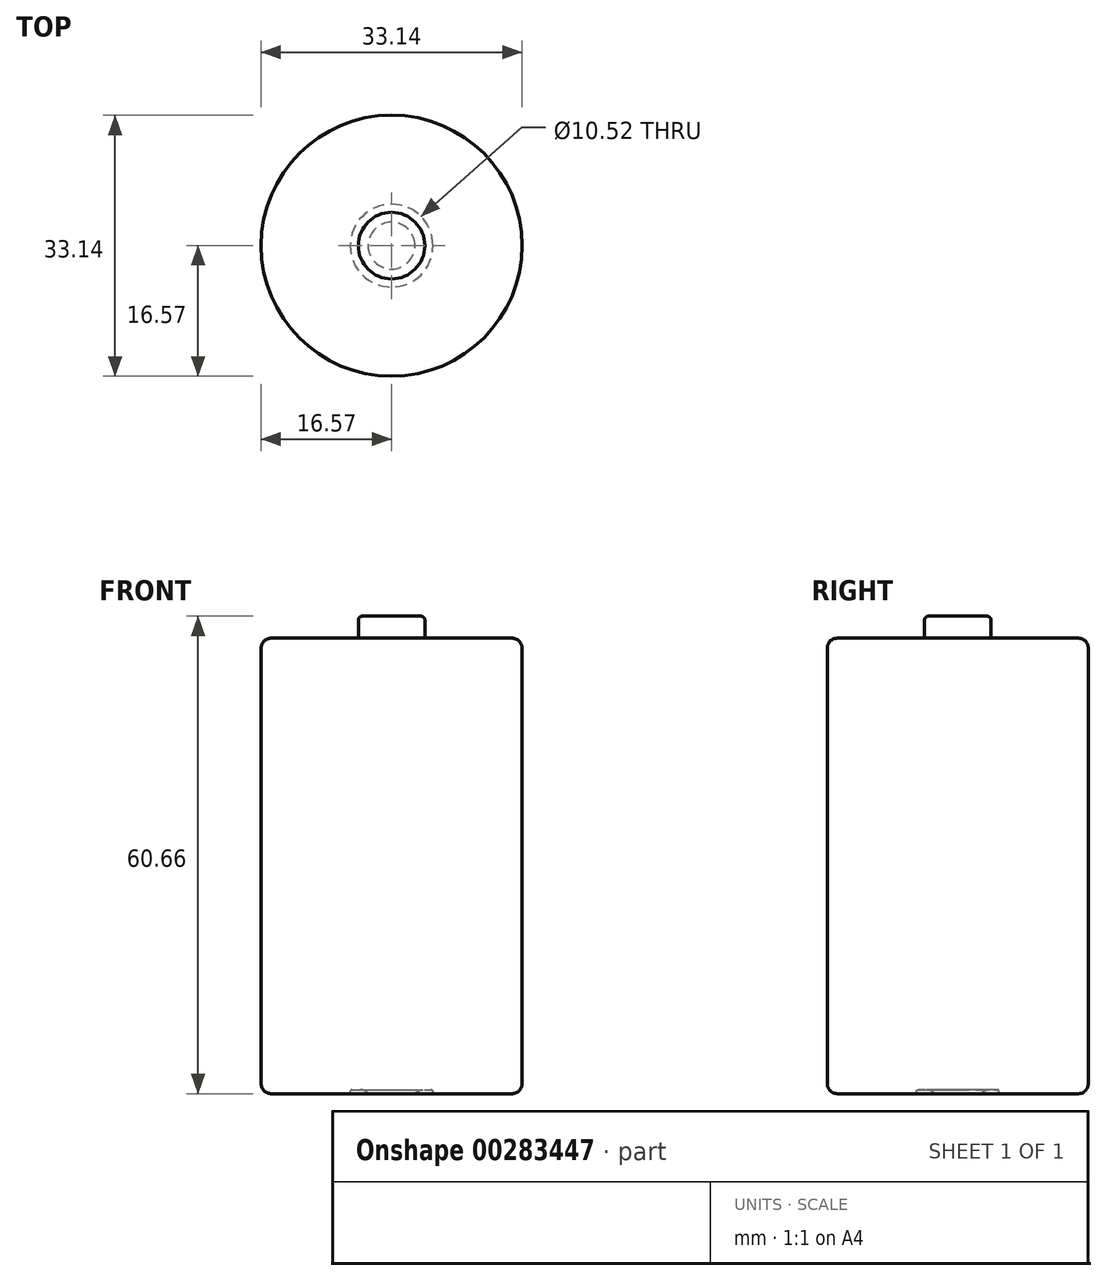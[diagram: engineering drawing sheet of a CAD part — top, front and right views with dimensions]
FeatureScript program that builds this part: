
annotation { "Feature Type Name" : "Feature", "Feature Type Description" : "" }
export const myFeature = defineFeature(function(context is Context, id is Id, definition is map)
    precondition{}
    {
        {
            var Q0;
            Q0=qCreatedBy(makeId("Top.planeOp"),FACE);
            var sketch = newSketch(context, id + "F0", { "sketchPlane" : qUnion([Q0])});
            skCircle(sketch, "E0", {"center": v(0, 0) * mm, "radius": 16.57 * mm});
            skSolve(sketch);
        }
        {
            var Q0;
            Q0=makeQuery(id+"F0.imprint","IMPRINT",FACE,{"disambiguationData":[TD([[makeQuery(id+"F0.imprint","IMPRINT",EDGE,{"derivedFrom":sQuery(id+"F0.wireOp",EDGE,"E0")}),1.0]])]});
            extrude(context, id + "F1", {"entities" : qUnion([Q0]), "depth" : 57.86 * mm});
        }
        {
            var Q0;
            Q0=makeQuery(id+"F1.opExtrude","CAP_FACE",FACE,{"disambiguationData":[OSD([sQuery(id+"F0.wireOp",EDGE,"E0")])],"isStart":false});
            var sketch = newSketch(context, id + "F2", { "sketchPlane" : qUnion([Q0])});
            skCircle(sketch, "E1", {"center": v(0, 0) * mm, "radius": 4.23 * mm});
            skSolve(sketch);
        }
        {
            var Q0;
            Q0=qSketchRegion(id+"F2",true);
            extrude(context, id + "F3", {"entities" : qUnion([Q0]), "operationType" : NewBodyOperationType.ADD, "depth" : 2.8 * mm});
        }
        {
            var Q0;
            Q0=makeQuery(id+"F3.opExtrude","CAP_EDGE",EDGE,{"disambiguationData":[OSD([sQuery(id+"F2.wireOp",EDGE,"E1")])],"isStart":false});
            var Q1;
            Q1=makeQuery(id+"F3.opExtrude","CAP_EDGE",EDGE,{"disambiguationData":[OSD([sQuery(id+"F2.wireOp",EDGE,"E1")])],"isStart":true});
            fillet(context, id + "F4", {"entities" : qUnion([Q0, Q1]), "radius" : 0.5 * mm, "tangentPropagation" : true, "allowEdgeOverflow" : false});
        }
        {
            var Q0;
            Q0=makeQuery(id+"F1.opExtrude","CAP_EDGE",EDGE,{"disambiguationData":[OSD([sQuery(id+"F0.wireOp",EDGE,"E0")])],"isStart":false});
            var Q1;
            Q1=makeQuery(id+"F1.opExtrude","CAP_EDGE",EDGE,{"disambiguationData":[OSD([sQuery(id+"F0.wireOp",EDGE,"E0")])],"isStart":true});
            fillet(context, id + "F5", {"entities" : qUnion([Q0, Q1]), "radius" : 1.27 * mm, "tangentPropagation" : true, "allowEdgeOverflow" : false});
        }
        {
            var Q0;
            Q0=makeQuery(id+"F1.opExtrude","CAP_FACE",FACE,{"disambiguationData":[OSD([sQuery(id+"F0.wireOp",EDGE,"E0")])],"isStart":true});
            var sketch = newSketch(context, id + "F6", { "sketchPlane" : qUnion([Q0])});
            skCircle(sketch, "E2", {"center": v(0, 0) * mm, "radius": 2.98 * mm});
            skCircle(sketch, "E3", {"center": v(0, 0) * mm, "radius": 5.26 * mm});
            skSolve(sketch);
        }
        {
            var Q0;
            Q0=makeQuery(id+"F6.imprint","IMPRINT",FACE,{"disambiguationData":[TD([[makeQuery(id+"F6.imprint","IMPRINT",EDGE,{"derivedFrom":sQuery(id+"F6.wireOp",EDGE,"E2")}),-1.0]])]});
            extrude(context, id + "F7", {"entities" : qUnion([Q0]), "operationType" : NewBodyOperationType.REMOVE, "oppositeDirection" : true, "depth" : 0.5 * mm});
        }
        {
            var Q0;
            Q0=makeQuery(id+"F7.boolean.opBoolean","COPY",EDGE,{"derivedFrom":makeQuery(id+"F7.opExtrude","CAP_EDGE",EDGE,{"disambiguationData":[OSD([sQuery(id+"F6.wireOp",EDGE,"E2")])],"isStart":false})});
            fillet(context, id + "F8", {"entities" : qUnion([Q0]), "radius" : 1.27 * mm, "tangentPropagation" : true, "allowEdgeOverflow" : false});
        }
        {
            var Q0;
            Q0=makeQuery(id+"F7.boolean.opBoolean","COPY",EDGE,{"derivedFrom":makeQuery(id+"F7.opExtrude","CAP_EDGE",EDGE,{"disambiguationData":[OSD([sQuery(id+"F6.wireOp",EDGE,"E3")])],"isStart":false})});
            var Q1;
            Q1=makeQuery(id+"F7.boolean.opBoolean","COPY",EDGE,{"derivedFrom":makeQuery(id+"F7.opExtrude","CAP_EDGE",EDGE,{"disambiguationData":[OSD([sQuery(id+"F6.wireOp",EDGE,"E3")])],"isStart":true})});
            fillet(context, id + "F9", {"entities" : qUnion([Q0, Q1]), "radius" : 0.25 * mm, "tangentPropagation" : true, "allowEdgeOverflow" : false});
        }
    });
